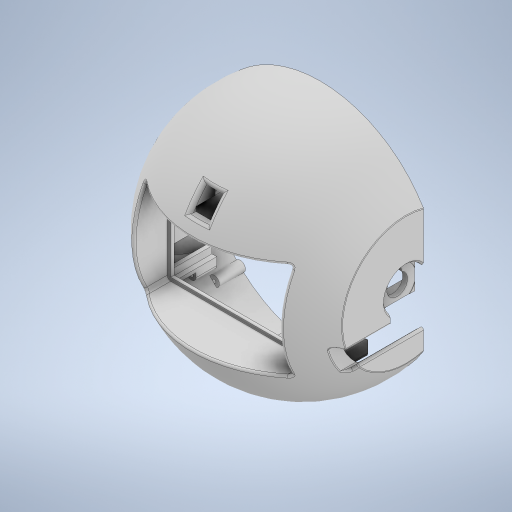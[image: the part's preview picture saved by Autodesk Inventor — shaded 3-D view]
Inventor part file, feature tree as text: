
AUTODESK INVENTOR PART (.ipt)
format: ipt  version: 2023 (Build 270158000, 158)  size: 1,131,008 bytes
history: native  units: mm
features: extrude x38, sketch x33, fillet x12, projected_geometry x9, other x4, chamfer x4, revolve x1, shell x1
ambient origin geometry x8: Origin, YZ Plane, XZ Plane, XY Plane, X Axis, Y Axis, Z Axis, Center Point
bodies: Body1 (feature_tree)
feature tree (102):
  other  "솔리드1"
  sketch  "스케치1"
  revolve  "회전1"
  other  "작업 평면1"
  extrude  "돌출2"  Depth=85.0mm
  other  "작업 평면2"
  extrude  "돌출3"  Depth=56.0mm
  shell  "쉘1"  Thickness=17.0mm
  extrude  "돌출4"  Depth=140.0mm
  extrude  "돌출5"  Depth=4.0mm
  extrude  "돌출6"  TaperAngle=360.0deg  [1 undecoded]
  extrude  "돌출7"  Depth=84.0mm
  extrude  "돌출8"  Depth=55.0mm
  extrude  "돌출9"  Depth=32.0mm TaperAngle=0.0deg
  extrude  "돌출10"  [1 undecoded]
  extrude  "돌출11"  Depth=165.25mm TaperAngle=0.0deg
  extrude  "돌출12"  Depth=4.0mm
  fillet  "모깎기1"  Radius=85.5mm
  extrude  "돌출13"  Depth=57.0mm
  sketch  "스케치16"
  extrude  "돌출14"  Depth=25.5mm TaperAngle=0.0deg
  extrude  "돌출16"  Depth=17.0mm TaperAngle=0.0deg
  fillet  "모깎기2"  Radius=16.5mm
  fillet  "모깎기3"  Radius=10.0mm
  fillet  "모깎기4"  Radius=18.5mm
  fillet  "모깎기5"  Radius=13.0mm
  extrude  "돌출17"  Depth=12.0mm
  sketch  "스케치19"
  extrude  "돌출19"  Depth=35.25mm TaperAngle=0.0deg
  extrude  "돌출20"  Depth=2.0mm
  extrude  "돌출21"  Depth=16.0mm TaperAngle=0.0deg
  sketch  "스케치22"
  extrude  "돌출22"  Depth=2.0mm
  extrude  "돌출24"  Depth=27.0mm
  extrude  "돌출26"  Depth=9.0mm
  extrude  "돌출27"  Depth=10.0mm TaperAngle=0.0deg
  extrude  "돌출28"  Depth=8.0mm
  fillet  "모깎기6"  Radius=23.0mm
  chamfer  "모따기3"  Distance=20.0mm
  extrude  "돌출29"  Depth=10.0mm TaperAngle=0.0deg
  extrude  "돌출30"  Depth=7.5mm
  extrude  "돌출31"  Depth=50.0mm
  extrude  "돌출32"  Depth=20.0mm TaperAngle=0.0deg
  fillet  "모깎기7"  Radius=2.0mm
  chamfer  "모따기6"  Distance=5.0mm
  chamfer  "모따기7"  Distance=5.0mm
  chamfer  "모따기8"  Distance=2.5mm
  fillet  "모깎기9"  Radius=12.0mm
  other  "작업 평면3"
  extrude  "돌출33"  Depth=0.5mm
  extrude  "돌출34"  Depth=1.0mm
  fillet  "모깎기14"  Radius=11.0mm
  extrude  "돌출42"  Depth=25.3mm
  extrude  "돌출43"  Depth=25.5mm TaperAngle=0.0deg
  extrude  "돌출44"  Depth=0.5mm
  fillet  "모깎기16"  Radius=2.0mm
  sketch  "스케치43"
  extrude  "돌출45"  Depth=15.0mm TaperAngle=0.0deg
  extrude  "돌출46"  Depth=80.0mm TaperAngle=360.0deg
  extrude  "돌출47"  Depth=12.5mm
  extrude  "돌출48"  Depth=23.1mm
  fillet  "모깎기17"  Radius=4.0mm
  fillet  "모깎기18"  Radius=4.55mm
  extrude  "돌출49"  Depth=12.0mm
  extrude  "돌출50"  Depth=12.0mm
  sketch  "스케치2"
  sketch  "스케치3"
  sketch  "스케치5"
  projected_geometry  "투영된 루프1"
  sketch  "스케치6"
  projected_geometry  "투영된 루프2"
  sketch  "스케치7"
  sketch  "스케치8"
  sketch  "스케치9"
  sketch  "스케치10"
  sketch  "스케치11"
  projected_geometry  "투영된 루프3"
  sketch  "스케치12"
  sketch  "스케치13"
  sketch  "스케치15"
  projected_geometry  "투영된 루프4"
  sketch  "스케치17"
  sketch  "스케치18"
  sketch  "스케치20"
  sketch  "스케치21"
  projected_geometry  "투영된 루프5"
  sketch  "스케치23"
  sketch  "스케치24"
  sketch  "스케치25"
  sketch  "스케치26"
  sketch  "스케치27"
  sketch  "스케치29"
  sketch  "스케치30"
  projected_geometry  "투영된 루프6"
  sketch  "스케치32"
  projected_geometry  "투영된 루프7"
  sketch  "스케치41"
  sketch  "스케치42"
  sketch  "스케치44"
  projected_geometry  "투영된 루프14"
  sketch  "스케치45"
  projected_geometry  "투영된 루프15"
note: 2 required parameter values undecoded (feature->parameter linkage not recoverable at this tier; creation-order binding heuristic only, values carry confidence <= 0.55)
